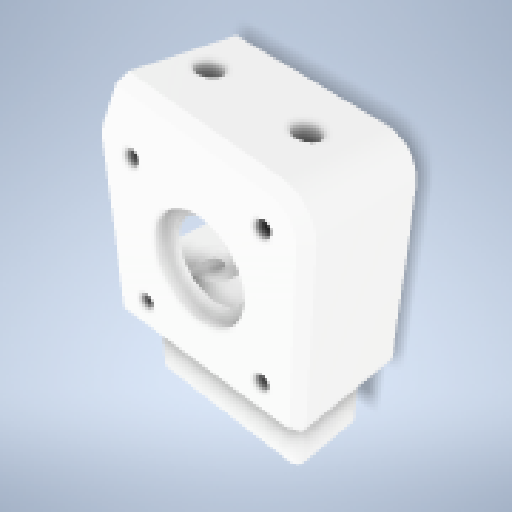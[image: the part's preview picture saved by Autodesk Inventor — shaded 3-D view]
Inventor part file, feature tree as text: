
AUTODESK INVENTOR PART (.ipt)
format: ipt  version: 2024 (Build 280153000, 153)  size: 557,056 bytes
history: native  units: mm
features: sketch x9, fillet x8, extrude x5, hole x5, projected_geometry x5, plane x2, chamfer x2
ambient origin geometry x8: Origin, YZ Plane, XZ Plane, XY Plane, X Axis, Y Axis, Z Axis, Center Point
bodies: Solid1 (feature_tree)
feature tree (36):
  extrude  "Extrusion1"  Depth=48.0mm
  hole  "Hole1"  [1 undecoded]
  extrude  "Extrusion2"  TaperAngle=150.0deg  [1 undecoded]
  sketch  "Sketch4"  dims[d6=28.0mm d7=0.0mm d8=31.0mm d9=31.0mm]
  plane  "Work Plane1"
  plane  "Work Plane2"
  extrude  "Extrusion4"  Depth=31.0mm
  fillet  "Fillet1"  Radius=31.0mm
  fillet  "Fillet2"  Radius=18.0mm
  chamfer  "Chamfer1"  [1 undecoded]
  extrude  "Extrusion5"  [1 undecoded]
  fillet  "Fillet8"  [1 undecoded]
  chamfer  "Chamfer3"  Distance=16.0mm
  hole  "Hole2"  [1 undecoded]
  extrude  "Extrusion8"  Depth=22.5mm
  hole  "Hole4"  [1 undecoded]
  sketch  "Sketch11"  dims[d33=2.5mm d34=0.0mm d39=6.5mm d40=6.0mm d41=4.0mm d42=2.0mm d43=90.0deg d44=6.5mm d45=0.0mm d67=3.0mm d68=2.0mm d69=2.0mm d70=45.0deg d73=18.0mm d74=40.0mm d75=14.0mm d76=0.0mm d79=9.0mm d80=9.0mm d81=9.0mm d82=9.0mm d83=22.0mm d84=5.3mm d85=6.0mm d86=4.0mm d87=2.0mm d88=90.0deg d89=10.0mm d90=0.0mm d91=10.0mm d92=6.0mm d93=4.0mm d94=2.0mm d95=90.0deg d96=10.0mm d97=0.0mm d98=5.0mm d99=6.0mm d100=4.0mm d101=2.0mm d102=90.0deg d103=8.0mm d104=0.0mm d105=2.0mm d106=1.0mm d107=1.0mm d108=1.0mm d109=0.5mm]
  hole  "Hole5"  [1 undecoded]
  hole  "Hole6"  [1 undecoded]
  fillet  "Fillet11"  Radius=40.0mm
  fillet  "Fillet12"  Radius=14.0mm
  fillet  "Fillet13"  Radius=9.0mm
  fillet  "Fillet14"  Radius=9.0mm
  fillet  "Fillet15"  Radius=9.0mm
  sketch  "Sketch1"  dims[d0=48.0mm d1=48.0mm]
  sketch  "Sketch2"  dims[d2=31.0mm d3=31.0mm]
  sketch  "Sketch3"  dims[d4=19.198622mm d5=150.0deg]
  sketch  "Sketch5"  dims[d10=3.3mm d11=6.0mm d12=4.0mm d13=2.0mm d14=90.0deg d15=8.0mm d16=20.594885mm d17=18.0mm d18=0.0mm d19=0.0mm]
  sketch  "Sketch6"  dims[d20=23.0mm d23=-3.75mm d24=-3.75mm d25=16.0mm d26=0.0mm]
  projected_geometry  "Projected Loop1"
  sketch  "Sketch9"  dims[d27=1.0mm d28=1.0mm]
  sketch  "Sketch10"  dims[d29=2.0mm d30=2.0mm d31=45.0deg d32=22.5mm]
  projected_geometry  "Projected Loop2"
  projected_geometry  "Projected Loop3"
  projected_geometry  "Projected Loop4"
  projected_geometry  "Project Cut Edges1"
note: 9 required parameter values undecoded (feature->parameter linkage not recoverable at this tier; creation-order binding heuristic only, values carry confidence <= 0.55)
